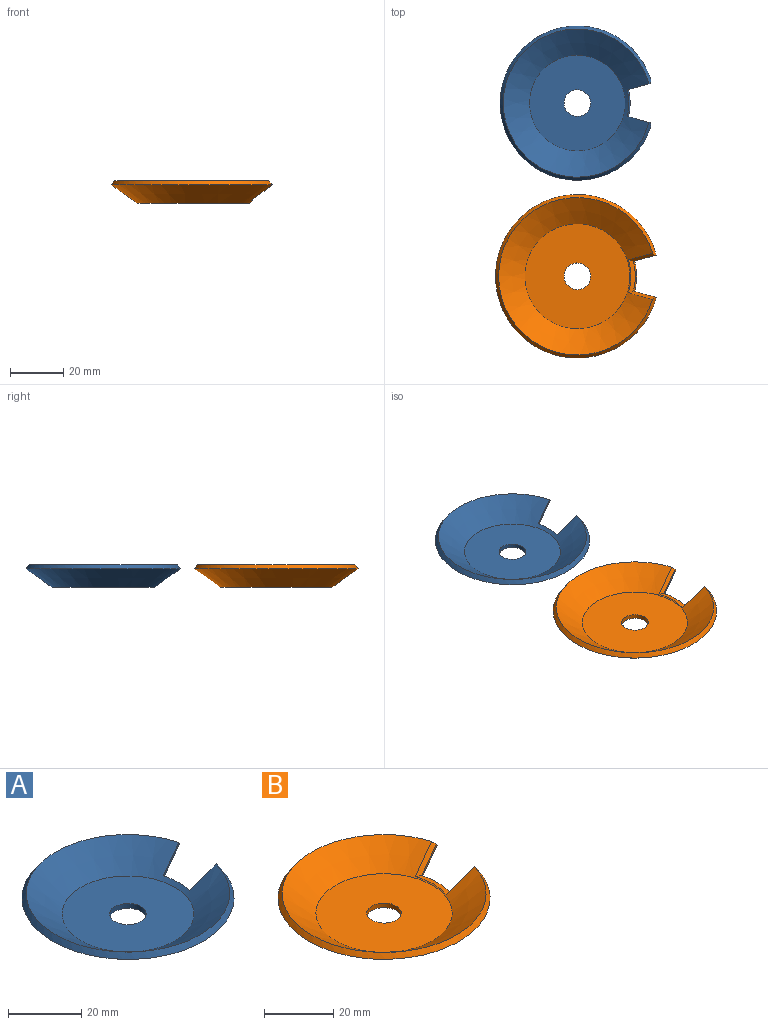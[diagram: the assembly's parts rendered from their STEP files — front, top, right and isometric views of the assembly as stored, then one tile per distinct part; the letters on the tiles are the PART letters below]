
ASSEMBLY  parts=2 mates=1
PART A: 12 faces, bbox 57.9x57.9x8.6 mm
  f0: cone r=27.81mm half-angle=54.7deg, axis (0,0,1), area 1599.5mm2, adj f1,f5,f6,f7,f8
  f1: plane 36.02x36.02mm, normal (0,0,1), area 940.7mm2, adj f0,f2
  f2: cylinder r=5mm len=10mm, axis (0,0,1), area 51.3mm2, adj f1,f3
  f3: plane 38.34x38.34mm, normal (0,0,-1), area 1075.7mm2, adj f2,f4
  f4: cone r=28.96mm half-angle=54.7deg, axis (0,0,1), area 1639.2mm2, adj f3,f5,f9,f10,f11
  f5: cone r=28.96mm half-angle=35.3deg, axis (0,0,-1), area 325.5mm2, adj f0,f4,f7,f8,f9,f11
  f6: cone r=20.51mm half-angle=35.3deg, axis (0,0,-1), area 8.2mm2, adj f0,f7,f8,f9,f10,f11
  f7: plane 8.6x6.62mm, normal (0.26,-0.97,0), area 8.1mm2, adj f0,f5,f6,f9
  f8: plane 8.6x6.62mm, normal (0.26,0.97,0), area 8.1mm2, adj f0,f5,f6,f11
  f9: bspline ~9.49x7.67mm, area 18.8mm2, adj f4,f5,f6,f7,f10
  f10: cone r=19.54mm half-angle=9.7deg, axis (0,0,1), area 19.6mm2, adj f4,f6,f9,f11
  f11: bspline ~9.49x7.67mm, area 18.8mm2, adj f4,f5,f6,f8,f10
PART B: 12 faces, bbox 61.4x61.4x8.9 mm
  f0: cone r=29.54mm half-angle=35.3deg, axis (0,0,-1), area 345.5mm2, adj f1,f5,f7,f8,f9,f11
  f1: cone r=19.75mm half-angle=54.7deg, axis (0,0,1), area 1680.9mm2, adj f0,f2,f9,f10,f11
  f2: plane 39.49x39.49mm, normal (0,0,1), area 1146.3mm2, adj f1,f3
  f3: cylinder r=5mm len=10mm, axis (0,0,1), area 51.3mm2, adj f2,f4
  f4: plane 41.8x41.8mm, normal (0,0,-1), area 1293.9mm2, adj f3,f5
  f5: cone r=30.7mm half-angle=54.7deg, axis (0,0,1), area 1801.7mm2, adj f0,f4,f6,f7,f8
  f6: cone r=22.25mm half-angle=35.3deg, axis (0,0,-1), area 9.4mm2, adj f5,f7,f8,f10
  f7: plane 8.63x6.66mm, normal (0.26,-0.97,0), area 8.5mm2, adj f0,f5,f6,f9
  f8: plane 8.62x6.65mm, normal (0.26,0.97,0), area 8.5mm2, adj f0,f5,f6,f11
  f9: bspline ~11.01x8.33mm, area 18.4mm2, adj f0,f1,f7,f10
  f10: cone r=21.79mm half-angle=80.3deg, axis (0,0,-1), area 20.2mm2, adj f1,f6,f9,f11
  f11: bspline ~11.01x8.33mm, area 18.4mm2, adj f0,f1,f8,f10
PLACE A t=(0,0,-11.8)mm
PLACE B t=(0,-65,-9.35)mm
MATE fastened B.f1 <-> A.f3  axis (0,0,-1) through (0,-65,0)mm
